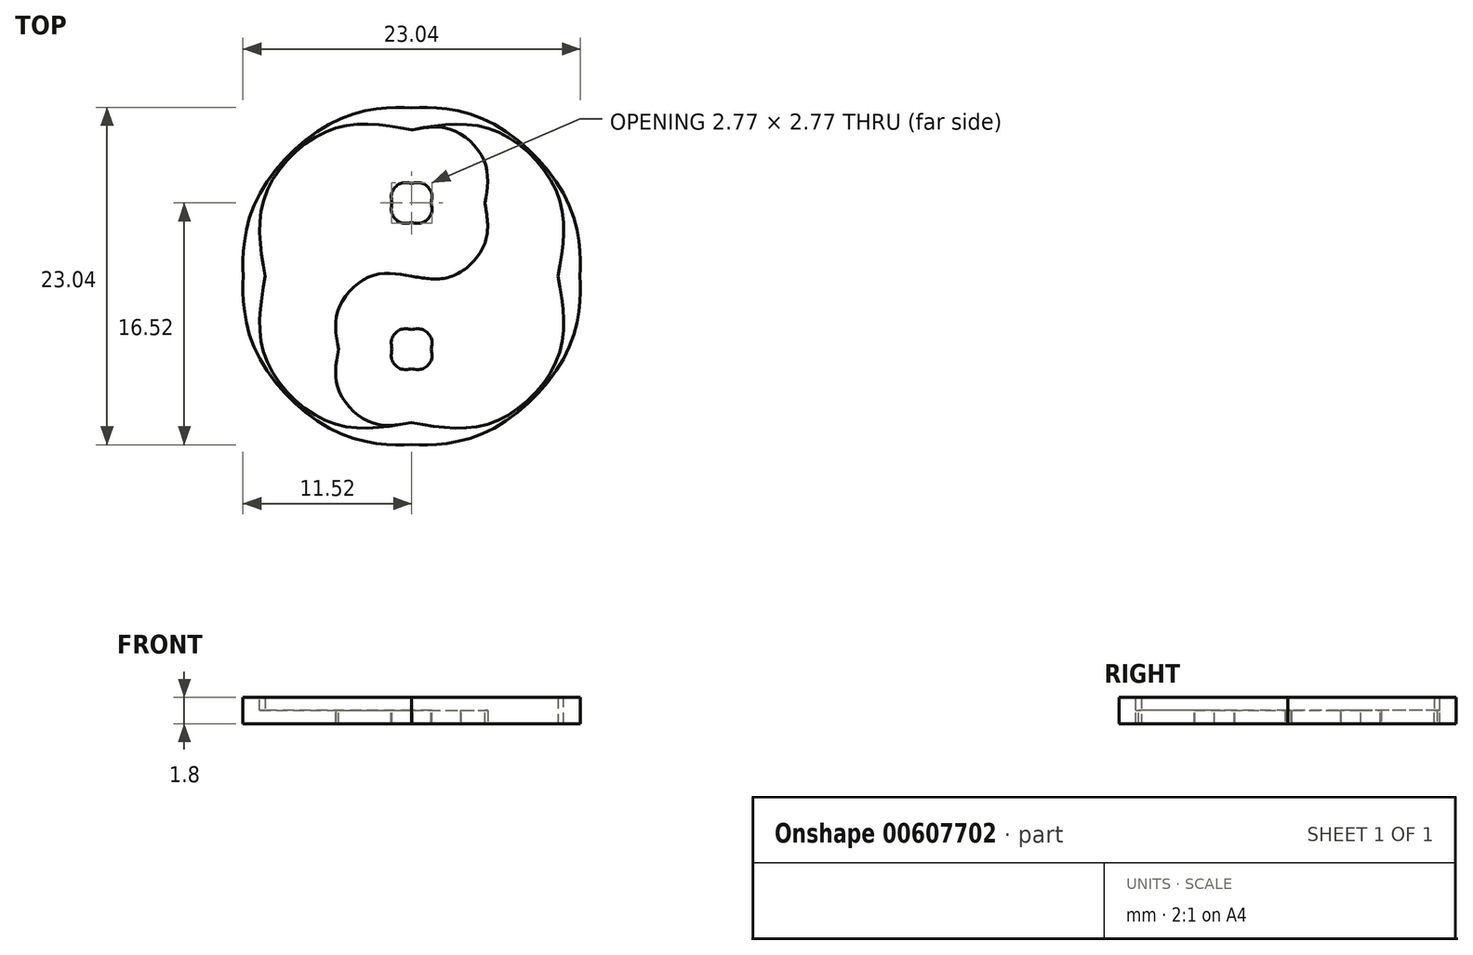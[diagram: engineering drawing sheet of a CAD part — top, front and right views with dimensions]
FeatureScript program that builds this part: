
annotation { "Feature Type Name" : "Feature", "Feature Type Description" : "" }
export const myFeature = defineFeature(function(context is Context, id is Id, definition is map)
    precondition{}
    {
        {
            var Q0;
            Q0=qCreatedBy(makeId("Top.planeOp"),FACE);
            var sketch = newSketch(context, id + "F0", { "sketchPlane" : qUnion([Q0])});
            skFitSpline(sketch, "E0", {"points": [v(0, 10) * mm, v(-5.52, 10) * mm, v(-10, 5.52) * mm, v(-10, 0) * mm]});
            skFitSpline(sketch, "E1", {"points": [v(-10, 0) * mm, v(-10, -5.52) * mm, v(-5.52, -10) * mm, v(0, -10) * mm]});
            skFitSpline(sketch, "E2", {"points": [v(0, -10) * mm, v(-2.76, -10) * mm, v(-5, -7.76) * mm, v(-5, -5) * mm]});
            skFitSpline(sketch, "E3", {"points": [v(-5, -5) * mm, v(-5, -2.24) * mm, v(-2.76, 0) * mm, v(0, 0) * mm]});
            skFitSpline(sketch, "E4", {"points": [v(0, 0) * mm, v(2.76, 0) * mm, v(5, 2.24) * mm, v(5, 5) * mm]});
            skFitSpline(sketch, "E5", {"points": [v(5, 5) * mm, v(5, 7.76) * mm, v(2.76, 10) * mm, v(0, 10) * mm]});
            skFitSpline(sketch, "E6", {"points": [v(0, 3.66) * mm, v(-0.74, 3.66) * mm, v(-1.34, 4.26) * mm, v(-1.34, 5) * mm]});
            skFitSpline(sketch, "E7", {"points": [v(-1.34, 5) * mm, v(-1.34, 5.74) * mm, v(-0.74, 6.34) * mm, v(0, 6.34) * mm]});
            skFitSpline(sketch, "E8", {"points": [v(0, 6.34) * mm, v(0.74, 6.34) * mm, v(1.34, 5.74) * mm, v(1.34, 5) * mm]});
            skFitSpline(sketch, "E9", {"points": [v(1.34, 5) * mm, v(1.34, 4.26) * mm, v(0.74, 3.66) * mm, v(0, 3.66) * mm]});
            skFitSpline(sketch, "E10", {"points": [v(-1.34, 5) * mm, v(-1.34, 5.74) * mm, v(-0.74, 6.34) * mm, v(0, 6.34) * mm]});
            skFitSpline(sketch, "E11", {"points": [v(0, 6.34) * mm, v(0.74, 6.34) * mm, v(1.34, 5.74) * mm, v(1.34, 5) * mm]});
            skFitSpline(sketch, "E12", {"points": [v(1.34, 5) * mm, v(1.34, 4.26) * mm, v(0.74, 3.66) * mm, v(0, 3.66) * mm]});
            skFitSpline(sketch, "E13", {"points": [v(0, 3.66) * mm, v(-0.74, 3.66) * mm, v(-1.34, 4.26) * mm, v(-1.34, 5) * mm]});
            skFitSpline(sketch, "E14", {"points": [v(0, 10) * mm, v(2.76, 10) * mm, v(5, 7.76) * mm, v(5, 5) * mm]});
            skFitSpline(sketch, "E15", {"points": [v(5, 5) * mm, v(5, 2.24) * mm, v(2.76, 0) * mm, v(0, 0) * mm]});
            skFitSpline(sketch, "E16", {"points": [v(0, 0) * mm, v(-2.76, 0) * mm, v(-5, -2.24) * mm, v(-5, -5) * mm]});
            skFitSpline(sketch, "E17", {"points": [v(-5, -5) * mm, v(-5, -7.76) * mm, v(-2.76, -10) * mm, v(0, -10) * mm]});
            skFitSpline(sketch, "E18", {"points": [v(0, -10) * mm, v(5.52, -10) * mm, v(10, -5.52) * mm, v(10, 0) * mm]});
            skFitSpline(sketch, "E19", {"points": [v(10, 0) * mm, v(10, 5.52) * mm, v(5.52, 10) * mm, v(0, 10) * mm]});
            skFitSpline(sketch, "E20", {"points": [v(0, -6.33) * mm, v(-0.74, -6.33) * mm, v(-1.34, -5.73) * mm, v(-1.34, -4.99) * mm]});
            skFitSpline(sketch, "E21", {"points": [v(-1.34, -4.99) * mm, v(-1.34, -4.25) * mm, v(-0.74, -3.65) * mm, v(0, -3.65) * mm]});
            skFitSpline(sketch, "E22", {"points": [v(0, -3.65) * mm, v(0.74, -3.65) * mm, v(1.34, -4.25) * mm, v(1.34, -4.99) * mm]});
            skFitSpline(sketch, "E23", {"points": [v(1.34, -4.99) * mm, v(1.34, -5.73) * mm, v(0.74, -6.33) * mm, v(0, -6.33) * mm]});
            skFitSpline(sketch, "E24", {"points": [v(1.34, 5) * mm, v(1.34, 4.26) * mm, v(0.74, 3.66) * mm, v(0, 3.66) * mm]});
            skFitSpline(sketch, "E25", {"points": [v(0, 3.66) * mm, v(-0.74, 3.66) * mm, v(-1.34, 4.26) * mm, v(-1.34, 5) * mm]});
            skFitSpline(sketch, "E26", {"points": [v(-1.34, 5) * mm, v(-1.34, 5.74) * mm, v(-0.74, 6.34) * mm, v(0, 6.34) * mm]});
            skFitSpline(sketch, "E27", {"points": [v(0, 6.34) * mm, v(0.74, 6.34) * mm, v(1.34, 5.74) * mm, v(1.34, 5) * mm]});
            skFitSpline(sketch, "E28", {"points": [v(1.34, 5) * mm, v(1.34, 4.26) * mm, v(0.74, 3.66) * mm, v(0, 3.66) * mm]});
            skFitSpline(sketch, "E29", {"points": [v(0, 3.66) * mm, v(-0.74, 3.66) * mm, v(-1.34, 4.26) * mm, v(-1.34, 5) * mm]});
            skFitSpline(sketch, "E30", {"points": [v(-1.34, 5) * mm, v(-1.34, 5.74) * mm, v(-0.74, 6.34) * mm, v(0, 6.34) * mm]});
            skFitSpline(sketch, "E31", {"points": [v(0, 6.34) * mm, v(0.74, 6.34) * mm, v(1.34, 5.74) * mm, v(1.34, 5) * mm]});
            skFitSpline(sketch, "E32.0", {"points": [v(0, 11.5) * mm, v(-1.58, 11.5) * mm, v(-4.62, 10.86) * mm, v(-8.33, 8.33) * mm, v(-10.86, 4.62) * mm, v(-11.5, 1.58) * mm, v(-11.5, 0) * mm]});
            skFitSpline(sketch, "E32.1", {"points": [v(11.5, 0) * mm, v(11.5, 1.58) * mm, v(10.86, 4.62) * mm, v(8.33, 8.33) * mm, v(4.62, 10.86) * mm, v(1.58, 11.5) * mm, v(0, 11.5) * mm]});
            skFitSpline(sketch, "E32.2", {"points": [v(0, -11.5) * mm, v(1.58, -11.5) * mm, v(4.62, -10.86) * mm, v(8.33, -8.33) * mm, v(10.86, -4.62) * mm, v(11.5, -1.58) * mm, v(11.5, 0) * mm]});
            skFitSpline(sketch, "E32.3", {"points": [v(-11.5, 0) * mm, v(-11.5, -1.58) * mm, v(-10.86, -4.62) * mm, v(-8.33, -8.33) * mm, v(-4.62, -10.86) * mm, v(-1.58, -11.5) * mm, v(0, -11.5) * mm]});
            skSolve(sketch);
        }
        {
            var Q0;
            Q0=makeQuery(id+"F0.imprint","IMPRINT",FACE,{"disambiguationData":[TD([[makeQuery(id+"F0.imprint","IMPRINT",EDGE,{"derivedFrom":sQuery(id+"F0.wireOp",EDGE,"E0")}),-1.0]])]});
            var Q1;
            Q1=makeQuery(id+"F0.imprint","IMPRINT",FACE,{"disambiguationData":[TD([[makeQuery(id+"F0.imprint","IMPRINT",EDGE,{"derivedFrom":sQuery(id+"F0.wireOp",EDGE,"E28")}),-1.0]])]});
            extrude(context, id + "F1", {"entities" : qUnion([Q0, Q1]), "depth" : 0.9 * mm, "offsetDistance" : 25 * mm});
        }
        {
            var Q0;
            Q0=makeQuery(id+"F1.opExtrude","CAP_FACE",FACE,{"disambiguationData":[OSD([sQuery(id+"F0.wireOp",EDGE,"E0"),sQuery(id+"F0.wireOp",EDGE,"E1"),sQuery(id+"F0.wireOp",EDGE,"E14"),sQuery(id+"F0.wireOp",EDGE,"E15"),sQuery(id+"F0.wireOp",EDGE,"E16"),sQuery(id+"F0.wireOp",EDGE,"E17"),sQuery(id+"F0.wireOp",EDGE,"E20"),sQuery(id+"F0.wireOp",EDGE,"E21"),sQuery(id+"F0.wireOp",EDGE,"E22"),sQuery(id+"F0.wireOp",EDGE,"E23"),sQuery(id+"F0.wireOp",EDGE,"E32.0"),sQuery(id+"F0.wireOp",EDGE,"E32.1"),sQuery(id+"F0.wireOp",EDGE,"E32.2"),sQuery(id+"F0.wireOp",EDGE,"E32.3")])],"isStart":true});
            var Q1;
            Q1=makeQuery(id+"F1.opExtrude","CAP_FACE",FACE,{"disambiguationData":[OSD([sQuery(id+"F0.wireOp",EDGE,"E28"),sQuery(id+"F0.wireOp",EDGE,"E29"),sQuery(id+"F0.wireOp",EDGE,"E30"),sQuery(id+"F0.wireOp",EDGE,"E31")])],"isStart":true});
            var Q2;
            {var subQ3=sQuery(id+"F0.wireOp",EDGE,"E0");Q2=makeQuery(id+"F0.imprint","IMPRINT",FACE,{"disambiguationData":[TD([[makeQuery(id+"F0.imprint","IMPRINT",EDGE,{"derivedFrom":subQ3}),1.0]])]});}
            var Q3;
            Q3=makeQuery(id+"F0.imprint","IMPRINT",FACE,{"disambiguationData":[TD([[makeQuery(id+"F0.imprint","IMPRINT",EDGE,{"derivedFrom":sQuery(id+"F0.wireOp",EDGE,"E20")}),-1.0]])]});
            extrude(context, id + "F2", {"entities" : qUnion([Q0, Q1, Q2, Q3]), "operationType" : NewBodyOperationType.ADD, "depth" : 0.9 * mm, "offsetDistance" : 25 * mm});
        }
    });
